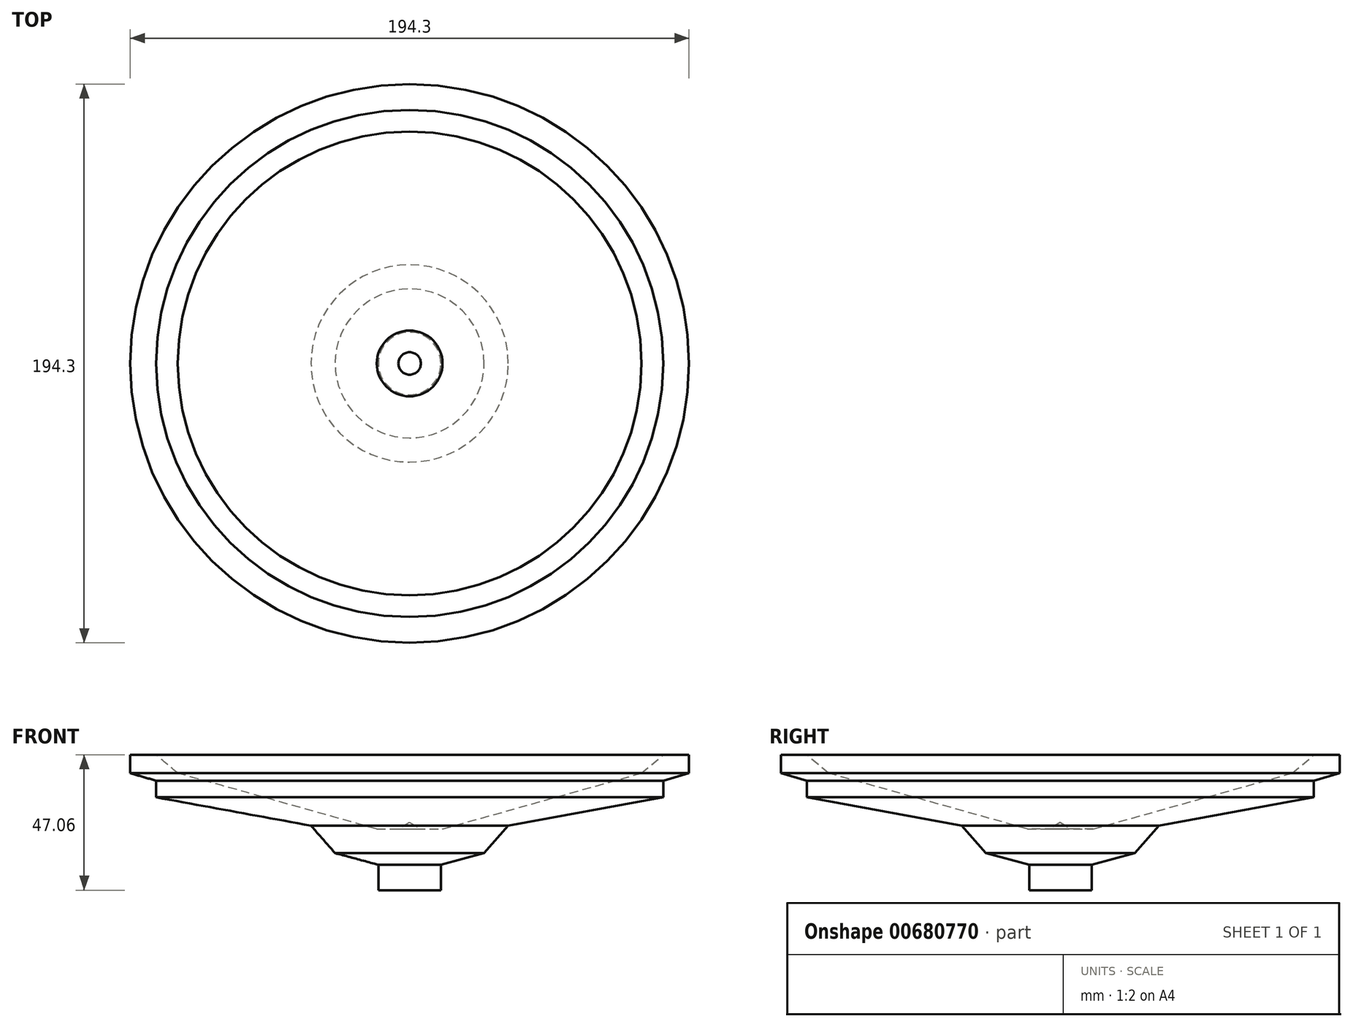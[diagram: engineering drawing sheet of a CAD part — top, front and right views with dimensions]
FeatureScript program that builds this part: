
annotation { "Feature Type Name" : "Feature", "Feature Type Description" : "" }
export const myFeature = defineFeature(function(context is Context, id is Id, definition is map)
    precondition{}
    {
        {
            var Q0;
            Q0=qCreatedBy(makeId("Front.planeOp"),FACE);
            var sketch = newSketch(context, id + "F0", { "sketchPlane" : qUnion([Q0])});
            skLineSegment(sketch, "E0", {"start": v(0, -75.72) * mm, "end": v(0, 112.79) * mm, "construction": true});
            skLineSegment(sketch, "E1", {"start": v(0, 0) * mm, "end": v(-10.86, 0) * mm});
            skLineSegment(sketch, "E2", {"start": v(-10.86, 0) * mm, "end": v(-10.86, 8.83) * mm});
            skLineSegment(sketch, "E3", {"start": v(-10.86, 8.83) * mm, "end": v(-25.92, 12.89) * mm});
            skLineSegment(sketch, "E4", {"start": v(-25.92, 12.89) * mm, "end": v(-34.31, 22.44) * mm});
            skLineSegment(sketch, "E5", {"start": v(-34.31, 22.44) * mm, "end": v(-88.18, 32.29) * mm});
            skLineSegment(sketch, "E6", {"start": v(-88.18, 32.29) * mm, "end": v(-88.18, 38.08) * mm});
            skLineSegment(sketch, "E7", {"start": v(-88.18, 38.08) * mm, "end": v(-97.15, 40.69) * mm});
            skLineSegment(sketch, "E8", {"start": v(-97.15, 40.69) * mm, "end": v(-97.15, 44.74) * mm});
            skLineSegment(sketch, "E9", {"start": v(-97.15, 44.74) * mm, "end": v(-97.15, 47.06) * mm});
            skLineSegment(sketch, "E10", {"start": v(-97.15, 47.06) * mm, "end": v(-88.18, 47.06) * mm});
            skLineSegment(sketch, "E11", {"start": v(-88.18, 47.06) * mm, "end": v(-80.65, 40.69) * mm});
            skLineSegment(sketch, "E12", {"start": v(-80.65, 40.69) * mm, "end": v(-11.44, 21.28) * mm});
            skLineSegment(sketch, "E13", {"start": v(-11.44, 21.28) * mm, "end": v(-3.9, 21.28) * mm});
            skLineSegment(sketch, "E14", {"start": v(-3.9, 21.28) * mm, "end": v(0, 23.6) * mm});
            skLineSegment(sketch, "E15", {"start": v(0, 23.6) * mm, "end": v(0, 0) * mm});
            skSolve(sketch);
        }
        {
            var Q0;
            Q0=makeQuery(id+"F0.imprint","IMPRINT",FACE,{"disambiguationData":[TD([[makeQuery(id+"F0.imprint","IMPRINT",EDGE,{"derivedFrom":sQuery(id+"F0.wireOp",EDGE,"E1")}),-1.0]])]});
            var Q1;
            Q1=sQuery(id+"F0.wireOp",EDGE,"E0");
            revolve(context, id + "F1", {"entities" : qUnion([Q0]), "axis" : qUnion([Q1]), "revolveType" : RevolveType.FULL});
        }
    });
